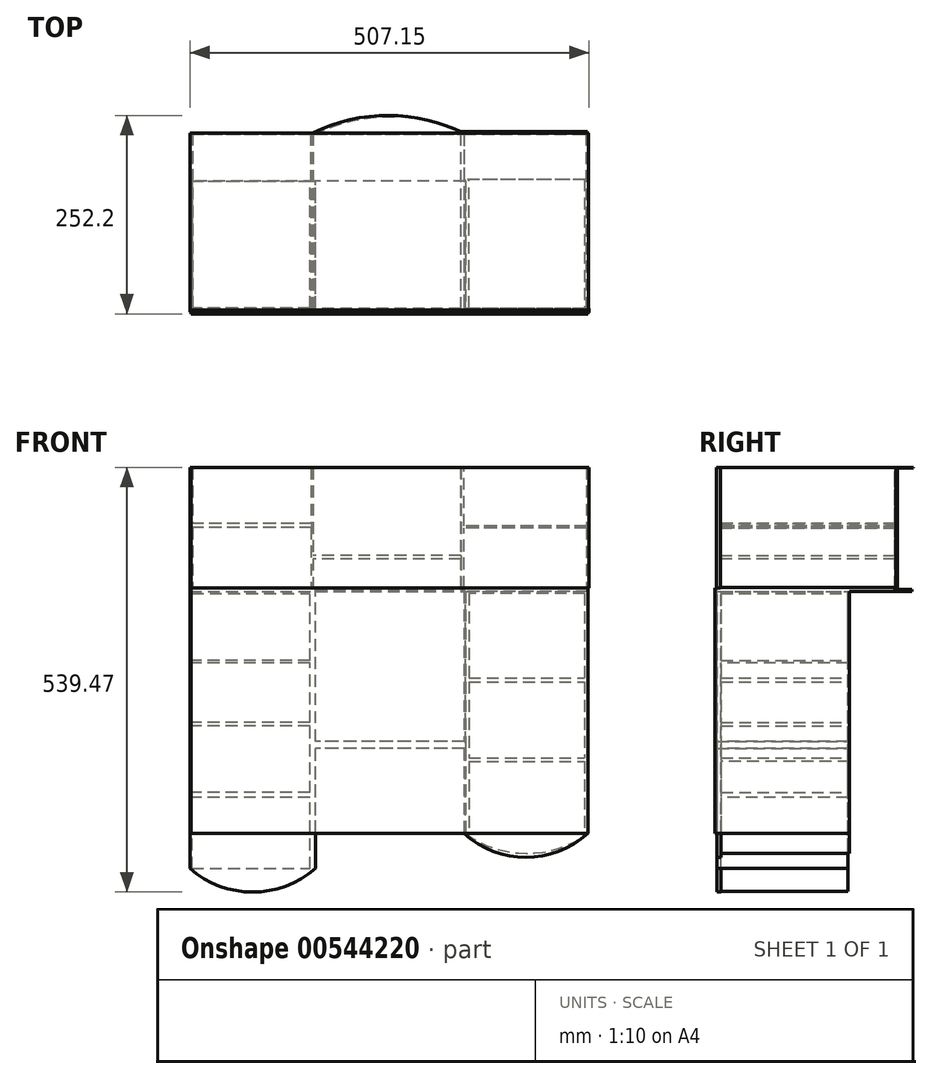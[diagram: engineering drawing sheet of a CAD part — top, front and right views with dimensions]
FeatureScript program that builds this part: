
annotation { "Feature Type Name" : "Feature", "Feature Type Description" : "" }
export const myFeature = defineFeature(function(context is Context, id is Id, definition is map)
    precondition{}
    {
        {
            var Q0;
            Q0=qCreatedBy(makeId("Top.planeOp"),FACE);
            var sketch = newSketch(context, id + "F0", { "sketchPlane" : qUnion([Q0])});
            skLineSegment(sketch, "E0.bottom", {"start": v(252.24, -140.99) * mm, "end": v(-253.83, -140.99) * mm});
            skLineSegment(sketch, "E0.top", {"start": v(252.24, 84.12) * mm, "end": v(-253.83, 84.12) * mm});
            skLineSegment(sketch, "E0.left", {"start": v(252.24, -140.99) * mm, "end": v(252.24, 84.12) * mm});
            skLineSegment(sketch, "E0.right", {"start": v(-253.83, -140.99) * mm, "end": v(-253.83, 84.12) * mm});
            skSolve(sketch);
        }
        {
            var Q0;
            Q0=makeQuery(id+"F0.imprint","IMPRINT",FACE,{"disambiguationData":[TD([[makeQuery(id+"F0.imprint","IMPRINT",EDGE,{"derivedFrom":sQuery(id+"F0.wireOp",EDGE,"E0.bottom")}),-1.0]])]});
            extrude(context, id + "F1", {"entities" : qUnion([Q0]), "depth" : 0.25 * mm, "offsetDistance" : 25.4 * mm});
        }
        {
            var Q0;
            Q0=makeQuery(id+"F1.opExtrude","CAP_FACE",FACE,{"disambiguationData":[OSD([sQuery(id+"F0.wireOp",EDGE,"E0.bottom"),sQuery(id+"F0.wireOp",EDGE,"E0.top"),sQuery(id+"F0.wireOp",EDGE,"E0.left"),sQuery(id+"F0.wireOp",EDGE,"E0.right")])],"isStart":true});
            var sketch = newSketch(context, id + "F2", { "sketchPlane" : qUnion([Q0])});
            skLineSegment(sketch, "E1", {"start": v(93.35, 140.99) * mm, "end": v(93.35, -84.12) * mm});
            skLineSegment(sketch, "E2", {"start": v(93.35, -84.12) * mm, "end": v(-97.43, -84.12) * mm});
            skLineSegment(sketch, "E3", {"start": v(-97.43, -84.12) * mm, "end": v(-97.43, 140.99) * mm});
            skSolve(sketch);
        }
        {
            var Q0;
            {var subQ0=sQuery(id+"F2.wireOp",EDGE,"E1");Q0=makeQuery(id+"F2.imprint","IMPRINT",FACE,{"disambiguationData":[TD([[makeQuery(id+"F2.imprint","IMPRINT",EDGE,{"derivedFrom":subQ0}),-1.0]])]});}
            var sketch = newSketch(context, id + "F3", { "sketchPlane" : qUnion([Q0])});
            skArc(sketch, "E4", {"start": v(-97.42, -84.86) * mm, "mid": v(-1.76, -106.5) * mm, "end": v(93.73, -84.09) * mm});
            skLineSegment(sketch, "E5", {"start": v(93.73, -84.09) * mm, "end": v(93.73, 141.67) * mm});
            skLineSegment(sketch, "E6", {"start": v(93.73, 141.67) * mm, "end": v(-97.17, 141.67) * mm});
            skLineSegment(sketch, "E7", {"start": v(-97.17, 141.67) * mm, "end": v(-97.42, -84.86) * mm});
            skSolve(sketch);
        }
        {
            var Q0;
            Q0 = qSketchRegion(id + "F3", true);
            extrude(context, id + "F4", {"entities" : qUnion([Q0]), "operationType" : NewBodyOperationType.ADD, "depth" : 0.25 * mm, "offsetDistance" : 25.4 * mm});
        }
        {
            var Q0;
            {var subQ0=sQuery(id+"F2.wireOp",EDGE,"E3");Q0=makeQuery(id+"F2.imprint","IMPRINT",FACE,{"disambiguationData":[TD([[makeQuery(id+"F2.imprint","IMPRINT",EDGE,{"derivedFrom":subQ0}),1.0]])]});}
            var sketch = newSketch(context, id + "F5", { "sketchPlane" : qUnion([Q0])});
            skLineSegment(sketch, "E8.bottom", {"start": v(-100.17, 141.24) * mm, "end": v(-98.13, 141.24) * mm});
            skLineSegment(sketch, "E8.top", {"start": v(-100.17, -83) * mm, "end": v(-98.13, -83) * mm});
            skLineSegment(sketch, "E8.left", {"start": v(-100.17, 141.24) * mm, "end": v(-100.17, -83) * mm});
            skLineSegment(sketch, "E8.right", {"start": v(-98.13, 141.24) * mm, "end": v(-98.13, -83) * mm});
            skSolve(sketch);
        }
        {
            var Q0;
            Q0 = qSketchRegion(id + "F5", true);
            extrude(context, id + "F6", {"entities" : qUnion([Q0]), "operationType" : NewBodyOperationType.ADD, "depth" : 152.4 * mm, "offsetDistance" : 25.4 * mm});
        }
        {
            var Q0;
            {var subQ0=sQuery(id+"F2.wireOp",EDGE,"E3");Q0=makeQuery(id+"F2.imprint","IMPRINT",FACE,{"disambiguationData":[TD([[makeQuery(id+"F2.imprint","IMPRINT",EDGE,{"derivedFrom":subQ0}),1.0]])]});}
            var sketch = newSketch(context, id + "F7", { "sketchPlane" : qUnion([Q0])});
            skLineSegment(sketch, "E9.bottom", {"start": v(-254.28, 140.62) * mm, "end": v(-250.99, 140.62) * mm});
            skLineSegment(sketch, "E9.top", {"start": v(-254.28, -84.03) * mm, "end": v(-250.99, -84.03) * mm});
            skLineSegment(sketch, "E9.left", {"start": v(-254.28, 140.62) * mm, "end": v(-254.28, -84.03) * mm});
            skLineSegment(sketch, "E9.right", {"start": v(-250.99, 140.62) * mm, "end": v(-250.99, -84.03) * mm});
            skSolve(sketch);
        }
        {
            var Q0;
            Q0 = qSketchRegion(id + "F7", true);
            extrude(context, id + "F8", {"entities" : qUnion([Q0]), "operationType" : NewBodyOperationType.ADD, "depth" : 152.4 * mm, "offsetDistance" : 25.4 * mm});
        }
        {
            var Q0;
            Q0=makeQuery(id+"F4.opExtrude","CAP_FACE",FACE,{"disambiguationData":[OSD([sQuery(id+"F3.wireOp",EDGE,"E4"),sQuery(id+"F3.wireOp",EDGE,"E5"),sQuery(id+"F3.wireOp",EDGE,"E6"),sQuery(id+"F3.wireOp",EDGE,"E7")])],"isStart":false});
            var sketch = newSketch(context, id + "F9", { "sketchPlane" : qUnion([Q0])});
            skLineSegment(sketch, "E10.bottom", {"start": v(93.73, 141.67) * mm, "end": v(89.91, 141.67) * mm});
            skLineSegment(sketch, "E10.top", {"start": v(93.73, -85.92) * mm, "end": v(89.91, -85.92) * mm});
            skLineSegment(sketch, "E10.left", {"start": v(93.73, 141.67) * mm, "end": v(93.73, -85.92) * mm});
            skLineSegment(sketch, "E10.right", {"start": v(89.91, 141.67) * mm, "end": v(89.91, -85.92) * mm});
            skSolve(sketch);
        }
        {
            var Q0;
            Q0 = qSketchRegion(id + "F9", true);
            extrude(context, id + "F10", {"entities" : qUnion([Q0]), "operationType" : NewBodyOperationType.ADD, "depth" : 152.4 * mm, "offsetDistance" : 25.4 * mm});
        }
        {
            var Q0;
            {var subQ0=sQuery(id+"F2.wireOp",EDGE,"E1");Q0=makeQuery(id+"F2.imprint","IMPRINT",FACE,{"disambiguationData":[TD([[makeQuery(id+"F2.imprint","IMPRINT",EDGE,{"derivedFrom":subQ0}),1.0]])]});}
            var sketch = newSketch(context, id + "F11", { "sketchPlane" : qUnion([Q0])});
            skLineSegment(sketch, "E11.bottom", {"start": v(251.96, 141.14) * mm, "end": v(249.44, 141.14) * mm});
            skLineSegment(sketch, "E11.top", {"start": v(251.96, -83.85) * mm, "end": v(249.44, -83.85) * mm});
            skLineSegment(sketch, "E11.left", {"start": v(251.96, 141.14) * mm, "end": v(251.96, -83.85) * mm});
            skLineSegment(sketch, "E11.right", {"start": v(249.44, 141.14) * mm, "end": v(249.44, -83.85) * mm});
            skSolve(sketch);
        }
        {
            var Q0;
            Q0 = qSketchRegion(id + "F11", true);
            extrude(context, id + "F12", {"entities" : qUnion([Q0]), "operationType" : NewBodyOperationType.ADD, "depth" : 152.4 * mm, "offsetDistance" : 25.4 * mm});
        }
        {
            var Q0;
            Q0=makeQuery(id+"F8.opExtrude","SWEPT_FACE",FACE,{"disambiguationData":[OSD([sQuery(id+"F7.wireOp",EDGE,"E9.right")])]});
            var sketch = newSketch(context, id + "F13", { "sketchPlane" : qUnion([Q0])});
            skLineSegment(sketch, "E12.bottom", {"start": v(84.03, -76.2) * mm, "end": v(-140.62, -76.2) * mm});
            skLineSegment(sketch, "E12.top", {"start": v(84.03, -70.9) * mm, "end": v(-140.62, -70.9) * mm});
            skLineSegment(sketch, "E12.left", {"start": v(84.03, -76.2) * mm, "end": v(84.03, -70.9) * mm});
            skLineSegment(sketch, "E12.right", {"start": v(-140.62, -76.2) * mm, "end": v(-140.62, -70.9) * mm});
            skSolve(sketch);
        }
        {
            var Q0;
            Q0 = qSketchRegion(id + "F13", true);
            extrude(context, id + "F14", {"entities" : qUnion([Q0]), "operationType" : NewBodyOperationType.ADD, "depth" : 151.9 * mm, "offsetDistance" : 25.4 * mm});
        }
        {
            var Q0;
            Q0=makeQuery(id+"F10.boolean.opBoolean","MERGE",FACE,{"derivedFrom":[makeQuery(id+"F4.opExtrude","SWEPT_FACE",FACE,{"disambiguationData":[OSD([sQuery(id+"F3.wireOp",EDGE,"E5")])]}),makeQuery(id+"F10.opExtrude","SWEPT_FACE",FACE,{"disambiguationData":[OSD([sQuery(id+"F9.wireOp",EDGE,"E10.left")])]})]});
            var sketch = newSketch(context, id + "F15", { "sketchPlane" : qUnion([Q0])});
            skLineSegment(sketch, "E13.bottom", {"start": v(85.92, -76.45) * mm, "end": v(-141.67, -76.45) * mm});
            skLineSegment(sketch, "E13.top", {"start": v(85.92, -74.03) * mm, "end": v(-141.67, -74.03) * mm});
            skLineSegment(sketch, "E13.left", {"start": v(85.92, -76.45) * mm, "end": v(85.92, -74.03) * mm});
            skLineSegment(sketch, "E13.right", {"start": v(-141.67, -76.45) * mm, "end": v(-141.67, -74.03) * mm});
            skSolve(sketch);
        }
        {
            var Q0;
            Q0 = qSketchRegion(id + "F15", true);
            extrude(context, id + "F16", {"entities" : qUnion([Q0]), "operationType" : NewBodyOperationType.ADD, "depth" : 157.23 * mm, "offsetDistance" : 25.4 * mm});
        }
        {
            var Q0;
            Q0=makeQuery(id+"F6.opExtrude","SWEPT_FACE",FACE,{"disambiguationData":[OSD([sQuery(id+"F5.wireOp",EDGE,"E8.right")])]});
            var sketch = newSketch(context, id + "F17", { "sketchPlane" : qUnion([Q0])});
            skLineSegment(sketch, "E14.bottom", {"start": v(83, -111.64) * mm, "end": v(-141.24, -111.64) * mm});
            skLineSegment(sketch, "E14.top", {"start": v(83, -115.78) * mm, "end": v(-141.24, -115.78) * mm});
            skLineSegment(sketch, "E14.left", {"start": v(83, -111.64) * mm, "end": v(83, -115.78) * mm});
            skLineSegment(sketch, "E14.right", {"start": v(-141.24, -111.64) * mm, "end": v(-141.24, -115.78) * mm});
            skSolve(sketch);
        }
        {
            var Q0;
            Q0 = qSketchRegion(id + "F17", true);
            extrude(context, id + "F18", {"entities" : qUnion([Q0]), "operationType" : NewBodyOperationType.ADD, "depth" : 189.74 * mm, "offsetDistance" : 25.4 * mm});
        }
        {
            var Q0;
            Q0=makeQuery(id+"F8.opExtrude","CAP_FACE",FACE,{"disambiguationData":[OSD([sQuery(id+"F7.wireOp",EDGE,"E9.bottom"),sQuery(id+"F7.wireOp",EDGE,"E9.top"),sQuery(id+"F7.wireOp",EDGE,"E9.left"),sQuery(id+"F7.wireOp",EDGE,"E9.right")])],"isStart":false});
            var sketch = newSketch(context, id + "F19", { "sketchPlane" : qUnion([Q0])});
            skLineSegment(sketch, "E15.bottom", {"start": v(-254.28, 140.62) * mm, "end": v(251.36, 140.62) * mm});
            skLineSegment(sketch, "E15.top", {"start": v(-254.28, -82.79) * mm, "end": v(251.36, -82.79) * mm});
            skLineSegment(sketch, "E15.left", {"start": v(-254.28, 140.62) * mm, "end": v(-254.28, -82.79) * mm});
            skLineSegment(sketch, "E15.right", {"start": v(251.36, 140.62) * mm, "end": v(251.36, -82.79) * mm});
            skSolve(sketch);
        }
        {
            var Q0;
            Q0 = qSketchRegion(id + "F19", true);
            extrude(context, id + "F20", {"entities" : qUnion([Q0]), "operationType" : NewBodyOperationType.ADD, "depth" : 2.54 * mm, "offsetDistance" : 25.4 * mm});
        }
        {
            var Q0;
            Q0=makeQuery(id+"F20.opExtrude","CAP_FACE",FACE,{"disambiguationData":[OSD([sQuery(id+"F19.wireOp",EDGE,"E15.bottom"),sQuery(id+"F19.wireOp",EDGE,"E15.top"),sQuery(id+"F19.wireOp",EDGE,"E15.left"),sQuery(id+"F19.wireOp",EDGE,"E15.right")])],"isStart":false});
            var sketch = newSketch(context, id + "F21", { "sketchPlane" : qUnion([Q0])});
            skArc(sketch, "E16", {"start": v(-94.65, -82.79) * mm, "mid": v(-0.1, -104.53) * mm, "end": v(94.44, -82.79) * mm});
            skLineSegment(sketch, "E17", {"start": v(94.44, -82.79) * mm, "end": v(94.44, 140.62) * mm});
            skLineSegment(sketch, "E18", {"start": v(94.44, 140.62) * mm, "end": v(-95.06, 140.62) * mm});
            skLineSegment(sketch, "E19", {"start": v(-95.06, 140.62) * mm, "end": v(-94.65, -82.79) * mm});
            skSolve(sketch);
        }
        {
            var Q0;
            Q0 = qSketchRegion(id + "F21", true);
            extrude(context, id + "F22", {"entities" : qUnion([Q0]), "operationType" : NewBodyOperationType.ADD, "depth" : 2.54 * mm, "offsetDistance" : 25.4 * mm});
        }
        {
            var Q0;
            {var subQ0=sQuery(id+"F19.wireOp",EDGE,"E15.bottom");var subQ1=sQuery(id+"F19.wireOp",EDGE,"E15.top");var subQ2=sQuery(id+"F19.wireOp",EDGE,"E15.right");Q0=makeQuery(id+"F22.boolean.opBoolean","SPLIT",FACE,{"disambiguationData":[TD([makeQuery(id+"F20.opExtrude","SWEPT_FACE",FACE,{"disambiguationData":[OSD([subQ2])]})])],"derivedFrom":makeQuery(id+"F20.opExtrude","CAP_FACE",FACE,{"disambiguationData":[OSD([subQ0,subQ1,sQuery(id+"F19.wireOp",EDGE,"E15.left"),subQ2])],"isStart":false})});}
            extrude(context, id + "F23", {"entities" : qUnion([Q0]), "operationType" : NewBodyOperationType.ADD, "depth" : 2.54 * mm, "offsetDistance" : 25.4 * mm});
        }
        {
            var Q0;
            {var subQ0=sQuery(id+"F19.wireOp",EDGE,"E15.bottom");var subQ1=sQuery(id+"F19.wireOp",EDGE,"E15.top");var subQ2=sQuery(id+"F19.wireOp",EDGE,"E15.left");Q0=makeQuery(id+"F22.boolean.opBoolean","SPLIT",FACE,{"disambiguationData":[TD([makeQuery(id+"F8.opExtrude","SWEPT_FACE",FACE,{"disambiguationData":[OSD([sQuery(id+"F7.wireOp",EDGE,"E9.left")])]})])],"derivedFrom":makeQuery(id+"F20.opExtrude","CAP_FACE",FACE,{"disambiguationData":[OSD([subQ0,subQ1,subQ2,sQuery(id+"F19.wireOp",EDGE,"E15.right")])],"isStart":false})});}
            extrude(context, id + "F24", {"entities" : qUnion([Q0]), "operationType" : NewBodyOperationType.ADD, "depth" : 2.54 * mm, "offsetDistance" : 25.4 * mm});
        }
        {
            var Q0;
            {var subQ0=sQuery(id+"F19.wireOp",EDGE,"E15.right");var subQ1=sQuery(id+"F19.wireOp",EDGE,"E15.left");var subQ2=sQuery(id+"F19.wireOp",EDGE,"E15.top");var subQ3=sQuery(id+"F19.wireOp",EDGE,"E15.bottom");Q0=makeQuery(id+"F24.boolean.opBoolean","MERGE",FACE,{"derivedFrom":[makeQuery(id+"F23.boolean.opBoolean","MERGE",FACE,{"derivedFrom":[makeQuery(id+"F22.opExtrude","CAP_FACE",FACE,{"disambiguationData":[OSD([sQuery(id+"F21.wireOp",EDGE,"E16"),sQuery(id+"F21.wireOp",EDGE,"E17"),sQuery(id+"F21.wireOp",EDGE,"E18"),sQuery(id+"F21.wireOp",EDGE,"E19")])],"isStart":false}),makeQuery(id+"F23.opExtrude","CAP_FACE",FACE,{"disambiguationData":[OSD([subQ3,subQ2,subQ1,subQ0])],"isStart":false})]}),makeQuery(id+"F24.opExtrude","CAP_FACE",FACE,{"disambiguationData":[OSD([subQ3,subQ2,subQ1,subQ0])],"isStart":false})]});}
            var sketch = newSketch(context, id + "F25", { "sketchPlane" : qUnion([Q0])});
            skLineSegment(sketch, "E20.bottom", {"start": v(-254.28, 140.62) * mm, "end": v(-94.65, 140.62) * mm});
            skLineSegment(sketch, "E20.top", {"start": v(-254.28, -23.27) * mm, "end": v(-94.65, -23.27) * mm});
            skLineSegment(sketch, "E20.left", {"start": v(-254.28, 140.62) * mm, "end": v(-254.28, -23.27) * mm});
            skLineSegment(sketch, "E20.right", {"start": v(-94.65, 140.62) * mm, "end": v(-94.65, -23.27) * mm});
            skSolve(sketch);
        }
        {
            var Q0;
            Q0 = qSketchRegion(id + "F25", true);
            extrude(context, id + "F26", {"entities" : qUnion([Q0]), "operationType" : NewBodyOperationType.ADD, "depth" : 2.54 * mm, "offsetDistance" : 25.4 * mm});
        }
        {
            var Q0;
            Q0=makeQuery(id+"F26.opExtrude","CAP_FACE",FACE,{"disambiguationData":[OSD([sQuery(id+"F25.wireOp",EDGE,"E20.bottom"),sQuery(id+"F25.wireOp",EDGE,"E20.top"),sQuery(id+"F25.wireOp",EDGE,"E20.left"),sQuery(id+"F25.wireOp",EDGE,"E20.right")])],"isStart":false});
            var sketch = newSketch(context, id + "F27", { "sketchPlane" : qUnion([Q0])});
            skLineSegment(sketch, "E21.bottom", {"start": v(-254.28, 140.62) * mm, "end": v(-251.77, 140.62) * mm});
            skLineSegment(sketch, "E21.top", {"start": v(-254.28, -23.27) * mm, "end": v(-251.77, -23.27) * mm});
            skLineSegment(sketch, "E21.left", {"start": v(-254.28, 140.62) * mm, "end": v(-254.28, -23.27) * mm});
            skLineSegment(sketch, "E21.right", {"start": v(-251.77, 140.62) * mm, "end": v(-251.77, -23.27) * mm});
            skSolve(sketch);
        }
        {
            var Q0;
            Q0 = qSketchRegion(id + "F27", true);
            extrude(context, id + "F28", {"entities" : qUnion([Q0]), "operationType" : NewBodyOperationType.ADD, "depth" : 349.25 * mm, "offsetDistance" : 25.4 * mm});
        }
        {
            var Q0;
            Q0=makeQuery(id+"F26.opExtrude","CAP_FACE",FACE,{"disambiguationData":[OSD([sQuery(id+"F25.wireOp",EDGE,"E20.bottom"),sQuery(id+"F25.wireOp",EDGE,"E20.top"),sQuery(id+"F25.wireOp",EDGE,"E20.left"),sQuery(id+"F25.wireOp",EDGE,"E20.right")])],"isStart":false});
            var sketch = newSketch(context, id + "F29", { "sketchPlane" : qUnion([Q0])});
            skLineSegment(sketch, "E22.bottom", {"start": v(-101.63, 140.62) * mm, "end": v(-94.65, 140.62) * mm});
            skLineSegment(sketch, "E22.top", {"start": v(-101.63, -23.27) * mm, "end": v(-94.65, -23.27) * mm});
            skLineSegment(sketch, "E22.left", {"start": v(-101.63, 140.62) * mm, "end": v(-101.63, -23.27) * mm});
            skLineSegment(sketch, "E22.right", {"start": v(-94.65, 140.62) * mm, "end": v(-94.65, -23.27) * mm});
            skSolve(sketch);
        }
        {
            var Q0;
            Q0 = qSketchRegion(id + "F29", true);
            extrude(context, id + "F30", {"entities" : qUnion([Q0]), "operationType" : NewBodyOperationType.ADD, "depth" : 349.25 * mm, "offsetDistance" : 25.4 * mm});
        }
        {
            var Q0;
            Q0=makeQuery(id+"F26.opExtrude","CAP_FACE",FACE,{"disambiguationData":[OSD([sQuery(id+"F25.wireOp",EDGE,"E20.bottom"),sQuery(id+"F25.wireOp",EDGE,"E20.top"),sQuery(id+"F25.wireOp",EDGE,"E20.left"),sQuery(id+"F25.wireOp",EDGE,"E20.right")])],"isStart":false});
            var sketch = newSketch(context, id + "F31", { "sketchPlane" : qUnion([Q0])});
            skLineSegment(sketch, "E23.bottom", {"start": v(-251.77, 140.62) * mm, "end": v(-101.63, 140.62) * mm});
            skLineSegment(sketch, "E23.top", {"start": v(-251.77, 137.96) * mm, "end": v(-101.63, 137.96) * mm});
            skLineSegment(sketch, "E23.left", {"start": v(-251.77, 140.62) * mm, "end": v(-251.77, 137.96) * mm});
            skLineSegment(sketch, "E23.right", {"start": v(-101.63, 140.62) * mm, "end": v(-101.63, 137.96) * mm});
            skSolve(sketch);
        }
        {
            var Q0;
            Q0 = qSketchRegion(id + "F31", true);
            extrude(context, id + "F32", {"entities" : qUnion([Q0]), "operationType" : NewBodyOperationType.ADD, "depth" : 349.25 * mm, "offsetDistance" : 25.4 * mm});
        }
        {
            var Q0;
            Q0=makeQuery(id+"F28.opExtrude","SWEPT_FACE",FACE,{"disambiguationData":[OSD([sQuery(id+"F27.wireOp",EDGE,"E21.right")])]});
            var sketch = newSketch(context, id + "F33", { "sketchPlane" : qUnion([Q0])});
            skLineSegment(sketch, "E24.bottom", {"start": v(-137.96, -244.9) * mm, "end": v(23.27, -244.9) * mm});
            skLineSegment(sketch, "E24.top", {"start": v(-137.96, -248.27) * mm, "end": v(23.27, -248.27) * mm});
            skLineSegment(sketch, "E24.left", {"start": v(-137.96, -244.9) * mm, "end": v(-137.96, -248.27) * mm});
            skLineSegment(sketch, "E24.right", {"start": v(23.27, -244.9) * mm, "end": v(23.27, -248.27) * mm});
            skSolve(sketch);
        }
        {
            var Q0;
            Q0 = qSketchRegion(id + "F33", true);
            extrude(context, id + "F34", {"entities" : qUnion([Q0]), "operationType" : NewBodyOperationType.ADD, "depth" : 154.7 * mm, "offsetDistance" : 25.4 * mm});
        }
        {
            var Q0;
            {var subQ2=sQuery(id+"F27.wireOp",EDGE,"E21.right");Q0=makeQuery(id+"F34.boolean.opBoolean","SPLIT",FACE,{"disambiguationData":[TD([makeQuery(id+"F34.opExtrude","SWEPT_FACE",FACE,{"disambiguationData":[OSD([sQuery(id+"F33.wireOp",EDGE,"E24.top")])]})])],"derivedFrom":makeQuery(id+"F28.opExtrude","SWEPT_FACE",FACE,{"disambiguationData":[OSD([subQ2])]})});}
            var sketch = newSketch(context, id + "F35", { "sketchPlane" : qUnion([Q0])});
            skLineSegment(sketch, "E25.bottom", {"start": v(23.27, -328.3) * mm, "end": v(-137.96, -328.3) * mm});
            skLineSegment(sketch, "E25.top", {"start": v(23.27, -323.66) * mm, "end": v(-137.96, -323.66) * mm});
            skLineSegment(sketch, "E25.left", {"start": v(23.27, -328.3) * mm, "end": v(23.27, -323.66) * mm});
            skLineSegment(sketch, "E25.right", {"start": v(-137.96, -328.3) * mm, "end": v(-137.96, -323.66) * mm});
            skSolve(sketch);
        }
        {
            var Q0;
            Q0 = qSketchRegion(id + "F35", true);
            extrude(context, id + "F36", {"entities" : qUnion([Q0]), "operationType" : NewBodyOperationType.ADD, "depth" : 154.94 * mm, "offsetDistance" : 25.4 * mm});
        }
        {
            var Q0;
            {var subQ4=sQuery(id+"F27.wireOp",EDGE,"E21.right");Q0=makeQuery(id+"F36.boolean.opBoolean","SPLIT",FACE,{"disambiguationData":[TD([makeQuery(id+"F36.opExtrude","SWEPT_FACE",FACE,{"disambiguationData":[OSD([sQuery(id+"F35.wireOp",EDGE,"E25.bottom")])]})])],"derivedFrom":makeQuery(id+"F34.boolean.opBoolean","SPLIT",FACE,{"disambiguationData":[TD([makeQuery(id+"F34.opExtrude","SWEPT_FACE",FACE,{"disambiguationData":[OSD([sQuery(id+"F33.wireOp",EDGE,"E24.top")])]})])],"derivedFrom":makeQuery(id+"F28.opExtrude","SWEPT_FACE",FACE,{"disambiguationData":[OSD([subQ4])]})})});}
            var sketch = newSketch(context, id + "F37", { "sketchPlane" : qUnion([Q0])});
            skLineSegment(sketch, "E26.bottom", {"start": v(23.27, -418.79) * mm, "end": v(-137.96, -418.79) * mm});
            skLineSegment(sketch, "E26.top", {"start": v(23.27, -412.73) * mm, "end": v(-137.96, -412.73) * mm});
            skLineSegment(sketch, "E26.left", {"start": v(23.27, -418.79) * mm, "end": v(23.27, -412.73) * mm});
            skLineSegment(sketch, "E26.right", {"start": v(-137.96, -418.79) * mm, "end": v(-137.96, -412.73) * mm});
            skSolve(sketch);
        }
        {
            var Q0;
            Q0 = qSketchRegion(id + "F37", true);
            extrude(context, id + "F38", {"entities" : qUnion([Q0]), "operationType" : NewBodyOperationType.ADD, "depth" : 154.94 * mm, "offsetDistance" : 25.4 * mm});
        }
        {
            var Q0;
            {var subQ0=sQuery(id+"F19.wireOp",EDGE,"E15.bottom");Q0=makeQuery(id+"F32.boolean.opBoolean","MERGE",FACE,{"derivedFrom":[makeQuery(id+"F30.boolean.opBoolean","MERGE",FACE,{"derivedFrom":[makeQuery(id+"F28.boolean.opBoolean","MERGE",FACE,{"derivedFrom":[makeQuery(id+"F26.boolean.opBoolean","MERGE",FACE,{"derivedFrom":[makeQuery(id+"F24.boolean.opBoolean","MERGE",FACE,{"derivedFrom":[makeQuery(id+"F23.boolean.opBoolean","MERGE",FACE,{"derivedFrom":[makeQuery(id+"F22.boolean.opBoolean","MERGE",FACE,{"derivedFrom":[makeQuery(id+"F20.boolean.opBoolean","MERGE",FACE,{"derivedFrom":[makeQuery(id+"F14.boolean.opBoolean","MERGE",FACE,{"derivedFrom":[makeQuery(id+"F8.opExtrude","SWEPT_FACE",FACE,{"disambiguationData":[OSD([sQuery(id+"F7.wireOp",EDGE,"E9.bottom")])]}),makeQuery(id+"F14.opExtrude","SWEPT_FACE",FACE,{"disambiguationData":[OSD([sQuery(id+"F13.wireOp",EDGE,"E12.right")])]})]}),makeQuery(id+"F20.opExtrude","SWEPT_FACE",FACE,{"disambiguationData":[OSD([subQ0])]})]}),makeQuery(id+"F22.opExtrude","SWEPT_FACE",FACE,{"disambiguationData":[OSD([sQuery(id+"F21.wireOp",EDGE,"E18")])]})]}),makeQuery(id+"F23.opExtrude","SWEPT_FACE",FACE,{"disambiguationData":[OSD([subQ0])]})]}),makeQuery(id+"F24.opExtrude","SWEPT_FACE",FACE,{"disambiguationData":[OSD([subQ0])]})]}),makeQuery(id+"F26.opExtrude","SWEPT_FACE",FACE,{"disambiguationData":[OSD([sQuery(id+"F25.wireOp",EDGE,"E20.bottom")])]})]}),makeQuery(id+"F28.opExtrude","SWEPT_FACE",FACE,{"disambiguationData":[OSD([sQuery(id+"F27.wireOp",EDGE,"E21.bottom")])]})]}),makeQuery(id+"F30.opExtrude","SWEPT_FACE",FACE,{"disambiguationData":[OSD([sQuery(id+"F29.wireOp",EDGE,"E22.bottom")])]})]}),makeQuery(id+"F32.opExtrude","SWEPT_FACE",FACE,{"disambiguationData":[OSD([sQuery(id+"F31.wireOp",EDGE,"E23.bottom")])]})]});}
            var sketch = newSketch(context, id + "F39", { "sketchPlane" : qUnion([Q0])});
            skArc(sketch, "E27", {"start": v(-254.28, -509.27) * mm, "mid": v(-174.47, -539.22) * mm, "end": v(-94.65, -509.27) * mm});
            skSolve(sketch);
        }
        {
            var Q0;
            Q0=makeQuery(id+"F39.imprint","IMPRINT",FACE,{"disambiguationData":[TD([[makeQuery(id+"F39.imprint","IMPRINT",EDGE,{"derivedFrom":sQuery(id+"F39.wireOp",EDGE,"E27")}),1.0]])]});
            extrude(context, id + "F40", {"entities" : qUnion([Q0]), "operationType" : NewBodyOperationType.ADD, "oppositeDirection" : true, "depth" : 2.54 * mm, "offsetDistance" : 25.4 * mm});
        }
        {
            var Q0;
            Q0=makeQuery(id+"F38.boolean.opBoolean","MERGE",FACE,{"derivedFrom":[makeQuery(id+"F36.boolean.opBoolean","MERGE",FACE,{"derivedFrom":[makeQuery(id+"F34.boolean.opBoolean","MERGE",FACE,{"derivedFrom":[makeQuery(id+"F30.boolean.opBoolean","MERGE",FACE,{"derivedFrom":[makeQuery(id+"F28.boolean.opBoolean","MERGE",FACE,{"derivedFrom":[makeQuery(id+"F26.opExtrude","SWEPT_FACE",FACE,{"disambiguationData":[OSD([sQuery(id+"F25.wireOp",EDGE,"E20.top")])]}),makeQuery(id+"F28.opExtrude","SWEPT_FACE",FACE,{"disambiguationData":[OSD([sQuery(id+"F27.wireOp",EDGE,"E21.top")])]})]}),makeQuery(id+"F30.opExtrude","SWEPT_FACE",FACE,{"disambiguationData":[OSD([sQuery(id+"F29.wireOp",EDGE,"E22.top")])]})]}),makeQuery(id+"F34.opExtrude","SWEPT_FACE",FACE,{"disambiguationData":[OSD([sQuery(id+"F33.wireOp",EDGE,"E24.right")])]})]}),makeQuery(id+"F36.opExtrude","SWEPT_FACE",FACE,{"disambiguationData":[OSD([sQuery(id+"F35.wireOp",EDGE,"E25.left")])]})]}),makeQuery(id+"F38.opExtrude","SWEPT_FACE",FACE,{"disambiguationData":[OSD([sQuery(id+"F37.wireOp",EDGE,"E26.left")])]})]});
            var sketch = newSketch(context, id + "F41", { "sketchPlane" : qUnion([Q0])});
            skArc(sketch, "E28", {"start": v(94.65, -509.27) * mm, "mid": v(174.47, -538.2) * mm, "end": v(254.28, -509.27) * mm});
            skLineSegment(sketch, "E29", {"start": v(94.65, -509.27) * mm, "end": v(254.28, -509.27) * mm});
            skSolve(sketch);
        }
        {
            var Q0;
            Q0 = qSketchRegion(id + "F41", true);
            extrude(context, id + "F42", {"entities" : qUnion([Q0]), "operationType" : NewBodyOperationType.ADD, "oppositeDirection" : true, "depth" : 2.54 * mm, "offsetDistance" : 25.4 * mm});
        }
        {
            var Q0;
            {var subQ0=sQuery(id+"F19.wireOp",EDGE,"E15.right");var subQ1=sQuery(id+"F19.wireOp",EDGE,"E15.left");var subQ2=sQuery(id+"F19.wireOp",EDGE,"E15.top");var subQ3=sQuery(id+"F19.wireOp",EDGE,"E15.bottom");Q0=makeQuery(id+"F24.boolean.opBoolean","MERGE",FACE,{"derivedFrom":[makeQuery(id+"F23.boolean.opBoolean","MERGE",FACE,{"derivedFrom":[makeQuery(id+"F22.opExtrude","CAP_FACE",FACE,{"disambiguationData":[OSD([sQuery(id+"F21.wireOp",EDGE,"E16"),sQuery(id+"F21.wireOp",EDGE,"E17"),sQuery(id+"F21.wireOp",EDGE,"E18"),sQuery(id+"F21.wireOp",EDGE,"E19")])],"isStart":false}),makeQuery(id+"F23.opExtrude","CAP_FACE",FACE,{"disambiguationData":[OSD([subQ3,subQ2,subQ1,subQ0])],"isStart":false})]}),makeQuery(id+"F24.opExtrude","CAP_FACE",FACE,{"disambiguationData":[OSD([subQ3,subQ2,subQ1,subQ0])],"isStart":false})]});}
            var sketch = newSketch(context, id + "F43", { "sketchPlane" : qUnion([Q0])});
            skLineSegment(sketch, "E30.bottom", {"start": v(251.36, 140.62) * mm, "end": v(95.75, 140.62) * mm});
            skLineSegment(sketch, "E30.top", {"start": v(251.36, -25.08) * mm, "end": v(95.75, -25.08) * mm});
            skLineSegment(sketch, "E30.left", {"start": v(251.36, 140.62) * mm, "end": v(251.36, -25.08) * mm});
            skLineSegment(sketch, "E30.right", {"start": v(95.75, 140.62) * mm, "end": v(95.75, -25.08) * mm});
            skSolve(sketch);
        }
        {
            var Q0;
            Q0 = qSketchRegion(id + "F43", true);
            extrude(context, id + "F44", {"entities" : qUnion([Q0]), "operationType" : NewBodyOperationType.ADD, "depth" : 2.54 * mm, "offsetDistance" : 25.4 * mm});
        }
        {
            var Q0;
            Q0=makeQuery(id+"F44.opExtrude","CAP_FACE",FACE,{"disambiguationData":[OSD([sQuery(id+"F43.wireOp",EDGE,"E30.bottom"),sQuery(id+"F43.wireOp",EDGE,"E30.top"),sQuery(id+"F43.wireOp",EDGE,"E30.left"),sQuery(id+"F43.wireOp",EDGE,"E30.right")])],"isStart":false});
            var sketch = newSketch(context, id + "F45", { "sketchPlane" : qUnion([Q0])});
            skLineSegment(sketch, "E31.bottom", {"start": v(247.23, 140.62) * mm, "end": v(251.36, 140.62) * mm});
            skLineSegment(sketch, "E31.top", {"start": v(247.23, -25.08) * mm, "end": v(251.36, -25.08) * mm});
            skLineSegment(sketch, "E31.left", {"start": v(247.23, 140.62) * mm, "end": v(247.23, -25.08) * mm});
            skLineSegment(sketch, "E31.right", {"start": v(251.36, 140.62) * mm, "end": v(251.36, -25.08) * mm});
            skSolve(sketch);
        }
        {
            var Q0;
            Q0 = qSketchRegion(id + "F45", true);
            extrude(context, id + "F46", {"entities" : qUnion([Q0]), "operationType" : NewBodyOperationType.ADD, "depth" : 304.8 * mm, "offsetDistance" : 25.4 * mm});
        }
        {
            var Q0;
            Q0=makeQuery(id+"F44.opExtrude","CAP_FACE",FACE,{"disambiguationData":[OSD([sQuery(id+"F43.wireOp",EDGE,"E30.bottom"),sQuery(id+"F43.wireOp",EDGE,"E30.top"),sQuery(id+"F43.wireOp",EDGE,"E30.left"),sQuery(id+"F43.wireOp",EDGE,"E30.right")])],"isStart":false});
            var sketch = newSketch(context, id + "F47", { "sketchPlane" : qUnion([Q0])});
            skLineSegment(sketch, "E32.bottom", {"start": v(95.75, 140.62) * mm, "end": v(100.09, 140.62) * mm});
            skLineSegment(sketch, "E32.top", {"start": v(95.75, -25.08) * mm, "end": v(100.09, -25.08) * mm});
            skLineSegment(sketch, "E32.left", {"start": v(95.75, 140.62) * mm, "end": v(95.75, -25.08) * mm});
            skLineSegment(sketch, "E32.right", {"start": v(100.09, 140.62) * mm, "end": v(100.09, -25.08) * mm});
            skSolve(sketch);
        }
        {
            var Q0;
            Q0 = qSketchRegion(id + "F47", true);
            extrude(context, id + "F48", {"entities" : qUnion([Q0]), "operationType" : NewBodyOperationType.ADD, "depth" : 304.8 * mm, "offsetDistance" : 25.4 * mm});
        }
        {
            var Q0;
            Q0=makeQuery(id+"F48.opExtrude","SWEPT_FACE",FACE,{"disambiguationData":[OSD([sQuery(id+"F47.wireOp",EDGE,"E32.right")])]});
            var sketch = newSketch(context, id + "F49", { "sketchPlane" : qUnion([Q0])});
            skLineSegment(sketch, "E33.bottom", {"start": v(-140.62, -267.1) * mm, "end": v(25.08, -267.1) * mm});
            skLineSegment(sketch, "E33.top", {"start": v(-140.62, -272.08) * mm, "end": v(25.08, -272.08) * mm});
            skLineSegment(sketch, "E33.left", {"start": v(-140.62, -267.1) * mm, "end": v(-140.62, -272.08) * mm});
            skLineSegment(sketch, "E33.right", {"start": v(25.08, -267.1) * mm, "end": v(25.08, -272.08) * mm});
            skSolve(sketch);
        }
        {
            var Q0;
            Q0 = qSketchRegion(id + "F49", true);
            extrude(context, id + "F50", {"entities" : qUnion([Q0]), "operationType" : NewBodyOperationType.ADD, "depth" : 149.86 * mm, "offsetDistance" : 25.4 * mm});
        }
        {
            var Q0;
            {var subQ6=sQuery(id+"F47.wireOp",EDGE,"E32.right");Q0=makeQuery(id+"F50.boolean.opBoolean","SPLIT",FACE,{"disambiguationData":[TD([makeQuery(id+"F50.opExtrude","SWEPT_FACE",FACE,{"disambiguationData":[OSD([sQuery(id+"F49.wireOp",EDGE,"E33.top")])]})])],"derivedFrom":makeQuery(id+"F48.opExtrude","SWEPT_FACE",FACE,{"disambiguationData":[OSD([subQ6])]})});}
            var sketch = newSketch(context, id + "F51", { "sketchPlane" : qUnion([Q0])});
            skLineSegment(sketch, "E34.bottom", {"start": v(-140.62, -368.45) * mm, "end": v(25.08, -368.45) * mm});
            skLineSegment(sketch, "E34.top", {"start": v(-140.62, -373.36) * mm, "end": v(25.08, -373.36) * mm});
            skLineSegment(sketch, "E34.left", {"start": v(-140.62, -368.45) * mm, "end": v(-140.62, -373.36) * mm});
            skLineSegment(sketch, "E34.right", {"start": v(25.08, -368.45) * mm, "end": v(25.08, -373.36) * mm});
            skSolve(sketch);
        }
        {
            var Q0;
            Q0 = qSketchRegion(id + "F51", true);
            extrude(context, id + "F52", {"entities" : qUnion([Q0]), "operationType" : NewBodyOperationType.ADD, "depth" : 149.86 * mm, "offsetDistance" : 25.4 * mm});
        }
        {
            var Q0;
            {var subQ0=sQuery(id+"F31.wireOp",EDGE,"E23.bottom");var subQ1=sQuery(id+"F29.wireOp",EDGE,"E22.bottom");var subQ2=sQuery(id+"F27.wireOp",EDGE,"E21.bottom");var subQ3=sQuery(id+"F19.wireOp",EDGE,"E15.bottom");Q0=makeQuery(id+"F52.boolean.opBoolean","MERGE",FACE,{"derivedFrom":[makeQuery(id+"F50.boolean.opBoolean","MERGE",FACE,{"derivedFrom":[makeQuery(id+"F48.boolean.opBoolean","MERGE",FACE,{"derivedFrom":[makeQuery(id+"F46.boolean.opBoolean","MERGE",FACE,{"derivedFrom":[makeQuery(id+"F44.boolean.opBoolean","MERGE",FACE,{"derivedFrom":[makeQuery(id+"F40.boolean.opBoolean","MERGE",FACE,{"derivedFrom":[makeQuery(id+"F32.boolean.opBoolean","MERGE",FACE,{"derivedFrom":[makeQuery(id+"F30.boolean.opBoolean","MERGE",FACE,{"derivedFrom":[makeQuery(id+"F28.boolean.opBoolean","MERGE",FACE,{"derivedFrom":[makeQuery(id+"F26.boolean.opBoolean","MERGE",FACE,{"derivedFrom":[makeQuery(id+"F24.boolean.opBoolean","MERGE",FACE,{"derivedFrom":[makeQuery(id+"F23.boolean.opBoolean","MERGE",FACE,{"derivedFrom":[makeQuery(id+"F22.boolean.opBoolean","MERGE",FACE,{"derivedFrom":[makeQuery(id+"F20.boolean.opBoolean","MERGE",FACE,{"derivedFrom":[makeQuery(id+"F14.boolean.opBoolean","MERGE",FACE,{"derivedFrom":[makeQuery(id+"F8.opExtrude","SWEPT_FACE",FACE,{"disambiguationData":[OSD([sQuery(id+"F7.wireOp",EDGE,"E9.bottom")])]}),makeQuery(id+"F14.opExtrude","SWEPT_FACE",FACE,{"disambiguationData":[OSD([sQuery(id+"F13.wireOp",EDGE,"E12.right")])]})]}),makeQuery(id+"F20.opExtrude","SWEPT_FACE",FACE,{"disambiguationData":[OSD([subQ3])]})]}),makeQuery(id+"F22.opExtrude","SWEPT_FACE",FACE,{"disambiguationData":[OSD([sQuery(id+"F21.wireOp",EDGE,"E18")])]})]}),makeQuery(id+"F23.opExtrude","SWEPT_FACE",FACE,{"disambiguationData":[OSD([subQ3])]})]}),makeQuery(id+"F24.opExtrude","SWEPT_FACE",FACE,{"disambiguationData":[OSD([subQ3])]})]}),makeQuery(id+"F26.opExtrude","SWEPT_FACE",FACE,{"disambiguationData":[OSD([sQuery(id+"F25.wireOp",EDGE,"E20.bottom")])]})]}),makeQuery(id+"F28.opExtrude","SWEPT_FACE",FACE,{"disambiguationData":[OSD([subQ2])]})]}),makeQuery(id+"F30.opExtrude","SWEPT_FACE",FACE,{"disambiguationData":[OSD([subQ1])]})]}),makeQuery(id+"F32.opExtrude","SWEPT_FACE",FACE,{"disambiguationData":[OSD([subQ0])]})]}),makeQuery(id+"F40.opExtrude","CAP_FACE",FACE,{"disambiguationData":[OSD([subQ2,subQ1,subQ0,sQuery(id+"F39.wireOp",EDGE,"E27")])],"isStart":true})]}),makeQuery(id+"F44.opExtrude","SWEPT_FACE",FACE,{"disambiguationData":[OSD([sQuery(id+"F43.wireOp",EDGE,"E30.bottom")])]})]}),makeQuery(id+"F46.opExtrude","SWEPT_FACE",FACE,{"disambiguationData":[OSD([sQuery(id+"F45.wireOp",EDGE,"E31.bottom")])]})]}),makeQuery(id+"F48.opExtrude","SWEPT_FACE",FACE,{"disambiguationData":[OSD([sQuery(id+"F47.wireOp",EDGE,"E32.bottom")])]})]}),makeQuery(id+"F50.opExtrude","SWEPT_FACE",FACE,{"disambiguationData":[OSD([sQuery(id+"F49.wireOp",EDGE,"E33.left")])]})]}),makeQuery(id+"F52.opExtrude","SWEPT_FACE",FACE,{"disambiguationData":[OSD([sQuery(id+"F51.wireOp",EDGE,"E34.left")])]})]});}
            var sketch = newSketch(context, id + "F53", { "sketchPlane" : qUnion([Q0])});
            skLineSegment(sketch, "E35.bottom", {"start": v(93.73, -152.4) * mm, "end": v(251.36, -152.4) * mm});
            skLineSegment(sketch, "E35.top", {"start": v(93.73, -464.82) * mm, "end": v(251.36, -464.82) * mm});
            skLineSegment(sketch, "E35.left", {"start": v(93.73, -152.4) * mm, "end": v(93.73, -464.82) * mm});
            skLineSegment(sketch, "E35.right", {"start": v(251.36, -152.4) * mm, "end": v(251.36, -464.82) * mm});
            skSolve(sketch);
        }
        {
            var Q0;
            Q0 = qSketchRegion(id + "F53", true);
            extrude(context, id + "F54", {"entities" : qUnion([Q0]), "operationType" : NewBodyOperationType.ADD, "oppositeDirection" : true, "depth" : 2.54 * mm, "offsetDistance" : 25.4 * mm});
        }
        {
            var Q0;
            {var subQ0=sQuery(id+"F31.wireOp",EDGE,"E23.bottom");var subQ1=sQuery(id+"F29.wireOp",EDGE,"E22.bottom");var subQ2=sQuery(id+"F27.wireOp",EDGE,"E21.bottom");var subQ3=sQuery(id+"F19.wireOp",EDGE,"E15.bottom");Q0=makeQuery(id+"F54.boolean.opBoolean","MERGE",FACE,{"derivedFrom":[makeQuery(id+"F52.boolean.opBoolean","MERGE",FACE,{"derivedFrom":[makeQuery(id+"F50.boolean.opBoolean","MERGE",FACE,{"derivedFrom":[makeQuery(id+"F48.boolean.opBoolean","MERGE",FACE,{"derivedFrom":[makeQuery(id+"F46.boolean.opBoolean","MERGE",FACE,{"derivedFrom":[makeQuery(id+"F44.boolean.opBoolean","MERGE",FACE,{"derivedFrom":[makeQuery(id+"F40.boolean.opBoolean","MERGE",FACE,{"derivedFrom":[makeQuery(id+"F32.boolean.opBoolean","MERGE",FACE,{"derivedFrom":[makeQuery(id+"F30.boolean.opBoolean","MERGE",FACE,{"derivedFrom":[makeQuery(id+"F28.boolean.opBoolean","MERGE",FACE,{"derivedFrom":[makeQuery(id+"F26.boolean.opBoolean","MERGE",FACE,{"derivedFrom":[makeQuery(id+"F24.boolean.opBoolean","MERGE",FACE,{"derivedFrom":[makeQuery(id+"F23.boolean.opBoolean","MERGE",FACE,{"derivedFrom":[makeQuery(id+"F22.boolean.opBoolean","MERGE",FACE,{"derivedFrom":[makeQuery(id+"F20.boolean.opBoolean","MERGE",FACE,{"derivedFrom":[makeQuery(id+"F14.boolean.opBoolean","MERGE",FACE,{"derivedFrom":[makeQuery(id+"F8.opExtrude","SWEPT_FACE",FACE,{"disambiguationData":[OSD([sQuery(id+"F7.wireOp",EDGE,"E9.bottom")])]}),makeQuery(id+"F14.opExtrude","SWEPT_FACE",FACE,{"disambiguationData":[OSD([sQuery(id+"F13.wireOp",EDGE,"E12.right")])]})]}),makeQuery(id+"F20.opExtrude","SWEPT_FACE",FACE,{"disambiguationData":[OSD([subQ3])]})]}),makeQuery(id+"F22.opExtrude","SWEPT_FACE",FACE,{"disambiguationData":[OSD([sQuery(id+"F21.wireOp",EDGE,"E18")])]})]}),makeQuery(id+"F23.opExtrude","SWEPT_FACE",FACE,{"disambiguationData":[OSD([subQ3])]})]}),makeQuery(id+"F24.opExtrude","SWEPT_FACE",FACE,{"disambiguationData":[OSD([subQ3])]})]}),makeQuery(id+"F26.opExtrude","SWEPT_FACE",FACE,{"disambiguationData":[OSD([sQuery(id+"F25.wireOp",EDGE,"E20.bottom")])]})]}),makeQuery(id+"F28.opExtrude","SWEPT_FACE",FACE,{"disambiguationData":[OSD([subQ2])]})]}),makeQuery(id+"F30.opExtrude","SWEPT_FACE",FACE,{"disambiguationData":[OSD([subQ1])]})]}),makeQuery(id+"F32.opExtrude","SWEPT_FACE",FACE,{"disambiguationData":[OSD([subQ0])]})]}),makeQuery(id+"F40.opExtrude","CAP_FACE",FACE,{"disambiguationData":[OSD([subQ2,subQ1,subQ0,sQuery(id+"F39.wireOp",EDGE,"E27")])],"isStart":true})]}),makeQuery(id+"F44.opExtrude","SWEPT_FACE",FACE,{"disambiguationData":[OSD([sQuery(id+"F43.wireOp",EDGE,"E30.bottom")])]})]}),makeQuery(id+"F46.opExtrude","SWEPT_FACE",FACE,{"disambiguationData":[OSD([sQuery(id+"F45.wireOp",EDGE,"E31.bottom")])]})]}),makeQuery(id+"F48.opExtrude","SWEPT_FACE",FACE,{"disambiguationData":[OSD([sQuery(id+"F47.wireOp",EDGE,"E32.bottom")])]})]}),makeQuery(id+"F50.opExtrude","SWEPT_FACE",FACE,{"disambiguationData":[OSD([sQuery(id+"F49.wireOp",EDGE,"E33.left")])]})]}),makeQuery(id+"F52.opExtrude","SWEPT_FACE",FACE,{"disambiguationData":[OSD([sQuery(id+"F51.wireOp",EDGE,"E34.left")])]})]}),makeQuery(id+"F54.opExtrude","CAP_FACE",FACE,{"disambiguationData":[OSD([sQuery(id+"F53.wireOp",EDGE,"E35.bottom"),sQuery(id+"F53.wireOp",EDGE,"E35.top"),sQuery(id+"F53.wireOp",EDGE,"E35.left"),sQuery(id+"F53.wireOp",EDGE,"E35.right")])],"isStart":true})]});}
            var sketch = newSketch(context, id + "F55", { "sketchPlane" : qUnion([Q0])});
            skArc(sketch, "E36", {"start": v(93.73, -464.82) * mm, "mid": v(172.54, -495.14) * mm, "end": v(251.36, -464.82) * mm});
            skLineSegment(sketch, "E37", {"start": v(93.73, -464.82) * mm, "end": v(251.36, -464.82) * mm});
            skSolve(sketch);
        }
        {
            var Q0;
            Q0 = qSketchRegion(id + "F55", true);
            extrude(context, id + "F56", {"entities" : qUnion([Q0]), "operationType" : NewBodyOperationType.ADD, "oppositeDirection" : true, "depth" : 2.54 * mm, "offsetDistance" : 25.4 * mm});
        }
        {
            var Q0;
            Q0=makeQuery(id+"F52.boolean.opBoolean","MERGE",FACE,{"derivedFrom":[makeQuery(id+"F50.boolean.opBoolean","MERGE",FACE,{"derivedFrom":[makeQuery(id+"F48.boolean.opBoolean","MERGE",FACE,{"derivedFrom":[makeQuery(id+"F46.boolean.opBoolean","MERGE",FACE,{"derivedFrom":[makeQuery(id+"F44.opExtrude","SWEPT_FACE",FACE,{"disambiguationData":[OSD([sQuery(id+"F43.wireOp",EDGE,"E30.top")])]}),makeQuery(id+"F46.opExtrude","SWEPT_FACE",FACE,{"disambiguationData":[OSD([sQuery(id+"F45.wireOp",EDGE,"E31.top")])]})]}),makeQuery(id+"F48.opExtrude","SWEPT_FACE",FACE,{"disambiguationData":[OSD([sQuery(id+"F47.wireOp",EDGE,"E32.top")])]})]}),makeQuery(id+"F50.opExtrude","SWEPT_FACE",FACE,{"disambiguationData":[OSD([sQuery(id+"F49.wireOp",EDGE,"E33.right")])]})]}),makeQuery(id+"F52.opExtrude","SWEPT_FACE",FACE,{"disambiguationData":[OSD([sQuery(id+"F51.wireOp",EDGE,"E34.right")])]})]});
            var sketch = newSketch(context, id + "F57", { "sketchPlane" : qUnion([Q0])});
            skArc(sketch, "E38", {"start": v(-251.36, -464.82) * mm, "mid": v(-173.56, -490.12) * mm, "end": v(-95.75, -464.82) * mm});
            skLineSegment(sketch, "E39", {"start": v(-95.75, -464.82) * mm, "end": v(-247.23, -464.82) * mm});
            skSolve(sketch);
        }
        {
            var Q0;
            {var subQ0=sQuery(id+"F57.wireOp",EDGE,"E38");Q0=makeQuery(id+"F57.imprint","IMPRINT",FACE,{"disambiguationData":[TD([[makeQuery(id+"F57.imprint","IMPRINT",EDGE,{"derivedFrom":subQ0}),1.0]])]});}
            extrude(context, id + "F58", {"entities" : qUnion([Q0]), "operationType" : NewBodyOperationType.ADD, "oppositeDirection" : true, "depth" : 2.54 * mm, "offsetDistance" : 25.4 * mm});
        }
        {
            var Q0;
            Q0=makeQuery(id+"F30.boolean.opBoolean","MERGE",FACE,{"derivedFrom":[makeQuery(id+"F26.opExtrude","SWEPT_FACE",FACE,{"disambiguationData":[OSD([sQuery(id+"F25.wireOp",EDGE,"E20.right")])]}),makeQuery(id+"F30.opExtrude","SWEPT_FACE",FACE,{"disambiguationData":[OSD([sQuery(id+"F29.wireOp",EDGE,"E22.right")])]})]});
            var sketch = newSketch(context, id + "F59", { "sketchPlane" : qUnion([Q0])});
            skLineSegment(sketch, "E40.bottom", {"start": v(-140.62, -347.56) * mm, "end": v(23.27, -347.56) * mm});
            skLineSegment(sketch, "E40.top", {"start": v(-140.62, -356.68) * mm, "end": v(23.27, -356.68) * mm});
            skLineSegment(sketch, "E40.left", {"start": v(-140.62, -347.56) * mm, "end": v(-140.62, -356.68) * mm});
            skLineSegment(sketch, "E40.right", {"start": v(23.27, -347.56) * mm, "end": v(23.27, -356.68) * mm});
            skSolve(sketch);
        }
        {
            var Q0;
            Q0 = qSketchRegion(id + "F59", true);
            extrude(context, id + "F60", {"entities" : qUnion([Q0]), "operationType" : NewBodyOperationType.ADD, "depth" : 191 * mm, "offsetDistance" : 25.4 * mm});
        }
        {
            var Q0;
            Q0=makeQuery(id+"F16.boolean.opBoolean","MERGE",FACE,{"derivedFrom":[makeQuery(id+"F10.boolean.opBoolean","MERGE",FACE,{"derivedFrom":[makeQuery(id+"F4.opExtrude","SWEPT_FACE",FACE,{"disambiguationData":[OSD([sQuery(id+"F3.wireOp",EDGE,"E6")])]}),makeQuery(id+"F10.opExtrude","SWEPT_FACE",FACE,{"disambiguationData":[OSD([sQuery(id+"F9.wireOp",EDGE,"E10.bottom")])]})]}),makeQuery(id+"F16.opExtrude","SWEPT_FACE",FACE,{"disambiguationData":[OSD([sQuery(id+"F15.wireOp",EDGE,"E13.right")])]})]});
            var sketch = newSketch(context, id + "F61", { "sketchPlane" : qUnion([Q0])});
            skLineSegment(sketch, "E41.bottom", {"start": v(252.87, 0) * mm, "end": v(-252.8, 0) * mm});
            skLineSegment(sketch, "E41.top", {"start": v(252.87, -152.65) * mm, "end": v(-252.8, -152.65) * mm});
            skLineSegment(sketch, "E41.left", {"start": v(252.87, 0) * mm, "end": v(252.87, -152.65) * mm});
            skLineSegment(sketch, "E41.right", {"start": v(-252.8, 0) * mm, "end": v(-252.8, -152.65) * mm});
            skSolve(sketch);
        }
        {
            var Q0;
            Q0 = qSketchRegion(id + "F61", true);
            extrude(context, id + "F62", {"entities" : qUnion([Q0]), "operationType" : NewBodyOperationType.ADD, "oppositeDirection" : true, "depth" : 2.54 * mm, "offsetDistance" : 25.4 * mm});
        }
        {
            var Q0;
            {var subQ0=sQuery(id+"F31.wireOp",EDGE,"E23.bottom");var subQ1=sQuery(id+"F29.wireOp",EDGE,"E22.bottom");var subQ2=sQuery(id+"F27.wireOp",EDGE,"E21.bottom");var subQ3=sQuery(id+"F19.wireOp",EDGE,"E15.bottom");Q0=makeQuery(id+"F60.boolean.opBoolean","MERGE",FACE,{"derivedFrom":[makeQuery(id+"F56.boolean.opBoolean","MERGE",FACE,{"derivedFrom":[makeQuery(id+"F54.boolean.opBoolean","MERGE",FACE,{"derivedFrom":[makeQuery(id+"F52.boolean.opBoolean","MERGE",FACE,{"derivedFrom":[makeQuery(id+"F50.boolean.opBoolean","MERGE",FACE,{"derivedFrom":[makeQuery(id+"F48.boolean.opBoolean","MERGE",FACE,{"derivedFrom":[makeQuery(id+"F46.boolean.opBoolean","MERGE",FACE,{"derivedFrom":[makeQuery(id+"F44.boolean.opBoolean","MERGE",FACE,{"derivedFrom":[makeQuery(id+"F40.boolean.opBoolean","MERGE",FACE,{"derivedFrom":[makeQuery(id+"F32.boolean.opBoolean","MERGE",FACE,{"derivedFrom":[makeQuery(id+"F30.boolean.opBoolean","MERGE",FACE,{"derivedFrom":[makeQuery(id+"F28.boolean.opBoolean","MERGE",FACE,{"derivedFrom":[makeQuery(id+"F26.boolean.opBoolean","MERGE",FACE,{"derivedFrom":[makeQuery(id+"F24.boolean.opBoolean","MERGE",FACE,{"derivedFrom":[makeQuery(id+"F23.boolean.opBoolean","MERGE",FACE,{"derivedFrom":[makeQuery(id+"F22.boolean.opBoolean","MERGE",FACE,{"derivedFrom":[makeQuery(id+"F20.boolean.opBoolean","MERGE",FACE,{"derivedFrom":[makeQuery(id+"F14.boolean.opBoolean","MERGE",FACE,{"derivedFrom":[makeQuery(id+"F8.opExtrude","SWEPT_FACE",FACE,{"disambiguationData":[OSD([sQuery(id+"F7.wireOp",EDGE,"E9.bottom")])]}),makeQuery(id+"F14.opExtrude","SWEPT_FACE",FACE,{"disambiguationData":[OSD([sQuery(id+"F13.wireOp",EDGE,"E12.right")])]})]}),makeQuery(id+"F20.opExtrude","SWEPT_FACE",FACE,{"disambiguationData":[OSD([subQ3])]})]}),makeQuery(id+"F22.opExtrude","SWEPT_FACE",FACE,{"disambiguationData":[OSD([sQuery(id+"F21.wireOp",EDGE,"E18")])]})]}),makeQuery(id+"F23.opExtrude","SWEPT_FACE",FACE,{"disambiguationData":[OSD([subQ3])]})]}),makeQuery(id+"F24.opExtrude","SWEPT_FACE",FACE,{"disambiguationData":[OSD([subQ3])]})]}),makeQuery(id+"F26.opExtrude","SWEPT_FACE",FACE,{"disambiguationData":[OSD([sQuery(id+"F25.wireOp",EDGE,"E20.bottom")])]})]}),makeQuery(id+"F28.opExtrude","SWEPT_FACE",FACE,{"disambiguationData":[OSD([subQ2])]})]}),makeQuery(id+"F30.opExtrude","SWEPT_FACE",FACE,{"disambiguationData":[OSD([subQ1])]})]}),makeQuery(id+"F32.opExtrude","SWEPT_FACE",FACE,{"disambiguationData":[OSD([subQ0])]})]}),makeQuery(id+"F40.opExtrude","CAP_FACE",FACE,{"disambiguationData":[OSD([subQ2,subQ1,subQ0,sQuery(id+"F39.wireOp",EDGE,"E27")])],"isStart":true})]}),makeQuery(id+"F44.opExtrude","SWEPT_FACE",FACE,{"disambiguationData":[OSD([sQuery(id+"F43.wireOp",EDGE,"E30.bottom")])]})]}),makeQuery(id+"F46.opExtrude","SWEPT_FACE",FACE,{"disambiguationData":[OSD([sQuery(id+"F45.wireOp",EDGE,"E31.bottom")])]})]}),makeQuery(id+"F48.opExtrude","SWEPT_FACE",FACE,{"disambiguationData":[OSD([sQuery(id+"F47.wireOp",EDGE,"E32.bottom")])]})]}),makeQuery(id+"F50.opExtrude","SWEPT_FACE",FACE,{"disambiguationData":[OSD([sQuery(id+"F49.wireOp",EDGE,"E33.left")])]})]}),makeQuery(id+"F52.opExtrude","SWEPT_FACE",FACE,{"disambiguationData":[OSD([sQuery(id+"F51.wireOp",EDGE,"E34.left")])]})]}),makeQuery(id+"F54.opExtrude","CAP_FACE",FACE,{"disambiguationData":[OSD([sQuery(id+"F53.wireOp",EDGE,"E35.bottom"),sQuery(id+"F53.wireOp",EDGE,"E35.top"),sQuery(id+"F53.wireOp",EDGE,"E35.left"),sQuery(id+"F53.wireOp",EDGE,"E35.right")])],"isStart":true})]}),makeQuery(id+"F56.opExtrude","CAP_FACE",FACE,{"disambiguationData":[OSD([sQuery(id+"F55.wireOp",EDGE,"E36"),sQuery(id+"F55.wireOp",EDGE,"E37")])],"isStart":true})]}),makeQuery(id+"F60.opExtrude","SWEPT_FACE",FACE,{"disambiguationData":[OSD([sQuery(id+"F59.wireOp",EDGE,"E40.left")])]})]});}
            extrude(context, id + "F63", {"entities" : qUnion([Q0]), "operationType" : NewBodyOperationType.ADD, "depth" : 2.54 * mm, "offsetDistance" : 25.4 * mm});
        }
        {
            var Q0;
            Q0=makeQuery(id+"F63.opExtrude","CAP_FACE",FACE,{"disambiguationData":[OSD([sQuery(id+"F7.wireOp",EDGE,"E9.bottom"),sQuery(id+"F13.wireOp",EDGE,"E12.right"),sQuery(id+"F19.wireOp",EDGE,"E15.bottom"),sQuery(id+"F21.wireOp",EDGE,"E18"),sQuery(id+"F25.wireOp",EDGE,"E20.bottom"),sQuery(id+"F27.wireOp",EDGE,"E21.bottom"),sQuery(id+"F29.wireOp",EDGE,"E22.bottom"),sQuery(id+"F31.wireOp",EDGE,"E23.bottom"),sQuery(id+"F39.wireOp",EDGE,"E27"),sQuery(id+"F43.wireOp",EDGE,"E30.bottom"),sQuery(id+"F45.wireOp",EDGE,"E31.bottom"),sQuery(id+"F47.wireOp",EDGE,"E32.bottom"),sQuery(id+"F49.wireOp",EDGE,"E33.left"),sQuery(id+"F51.wireOp",EDGE,"E34.left"),sQuery(id+"F53.wireOp",EDGE,"E35.bottom"),sQuery(id+"F53.wireOp",EDGE,"E35.top"),sQuery(id+"F53.wireOp",EDGE,"E35.left"),sQuery(id+"F53.wireOp",EDGE,"E35.right"),sQuery(id+"F55.wireOp",EDGE,"E36"),sQuery(id+"F55.wireOp",EDGE,"E37"),sQuery(id+"F59.wireOp",EDGE,"E40.left")])],"isStart":false});
            var sketch = newSketch(context, id + "F64", { "sketchPlane" : qUnion([Q0])});
            skLineSegment(sketch, "E42.bottom", {"start": v(251.36, -464.82) * mm, "end": v(-252.8, -464.82) * mm});
            skLineSegment(sketch, "E42.top", {"start": v(251.36, -152.65) * mm, "end": v(-252.8, -152.65) * mm});
            skLineSegment(sketch, "E42.left", {"start": v(251.36, -464.82) * mm, "end": v(251.36, -152.65) * mm});
            skLineSegment(sketch, "E42.right", {"start": v(-252.8, -464.82) * mm, "end": v(-252.8, -152.65) * mm});
            skSolve(sketch);
        }
        {
            var Q0;
            Q0 = qSketchRegion(id + "F64", true);
            extrude(context, id + "F65", {"entities" : qUnion([Q0]), "operationType" : NewBodyOperationType.ADD, "depth" : 2.54 * mm, "offsetDistance" : 25.4 * mm});
        }
        {
            var Q0;
            Q0=makeQuery(id+"F62.boolean.opBoolean","MERGE",FACE,{"derivedFrom":[makeQuery(id+"F16.boolean.opBoolean","MERGE",FACE,{"derivedFrom":[makeQuery(id+"F10.boolean.opBoolean","MERGE",FACE,{"derivedFrom":[makeQuery(id+"F4.opExtrude","SWEPT_FACE",FACE,{"disambiguationData":[OSD([sQuery(id+"F3.wireOp",EDGE,"E6")])]}),makeQuery(id+"F10.opExtrude","SWEPT_FACE",FACE,{"disambiguationData":[OSD([sQuery(id+"F9.wireOp",EDGE,"E10.bottom")])]})]}),makeQuery(id+"F16.opExtrude","SWEPT_FACE",FACE,{"disambiguationData":[OSD([sQuery(id+"F15.wireOp",EDGE,"E13.right")])]})]}),makeQuery(id+"F62.opExtrude","CAP_FACE",FACE,{"disambiguationData":[OSD([sQuery(id+"F61.wireOp",EDGE,"E41.bottom"),sQuery(id+"F61.wireOp",EDGE,"E41.top"),sQuery(id+"F61.wireOp",EDGE,"E41.left"),sQuery(id+"F61.wireOp",EDGE,"E41.right")])],"isStart":true})]});
            extrude(context, id + "F66", {"entities" : qUnion([Q0]), "operationType" : NewBodyOperationType.ADD, "depth" : 2.54 * mm, "offsetDistance" : 25.4 * mm});
        }
        {
            var Q0;
            Q0=makeQuery(id+"F58.opExtrude","CAP_FACE",FACE,{"disambiguationData":[OSD([sQuery(id+"F45.wireOp",EDGE,"E31.top"),sQuery(id+"F57.wireOp",EDGE,"E38"),sQuery(id+"F57.wireOp",EDGE,"E39")])],"isStart":false});
            extrude(context, id + "F67", {"entities" : qUnion([Q0]), "operationType" : NewBodyOperationType.ADD, "depth" : 162.56 * mm, "offsetDistance" : 25.4 * mm});
        }
        {
            var Q0;
            Q0=makeQuery(id+"F42.opExtrude","CAP_FACE",FACE,{"disambiguationData":[OSD([sQuery(id+"F41.wireOp",EDGE,"E28"),sQuery(id+"F41.wireOp",EDGE,"E29")])],"isStart":false});
            extrude(context, id + "F68", {"entities" : qUnion([Q0]), "operationType" : NewBodyOperationType.ADD, "depth" : 162.56 * mm, "offsetDistance" : 25.4 * mm});
        }
    });
